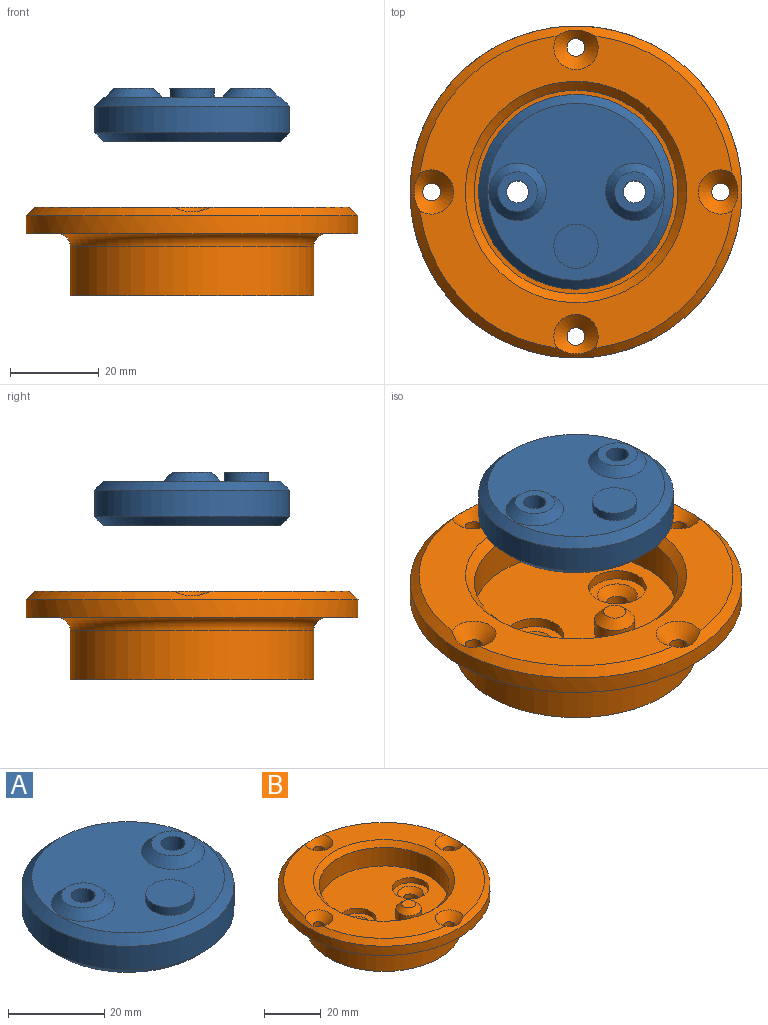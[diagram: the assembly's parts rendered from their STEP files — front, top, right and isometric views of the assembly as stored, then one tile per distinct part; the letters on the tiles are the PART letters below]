
ASSEMBLY  parts=2 mates=1
PART A: 22 faces, bbox 44x44x12 mm
  f0: cylinder r=5mm len=10mm, axis (0,0,-1), area 141.4mm2, adj f14,f15
  f1: cylinder r=6.5mm len=13mm, axis (0,0,-1), area 112.3mm2, adj f5,f11
  f2: cylinder r=6.5mm len=13mm, axis (0,0,-1), area 112.3mm2, adj f5,f8
  f3: cylinder r=22mm len=44mm, axis (0,0,-1), area 829.4mm2, adj f18,f19
  f4: plane 40x40mm, normal (0,0,1), area 912.6mm2, adj f13,f19,f20,f21
  f5: plane 40x40mm, normal (0,0,-1), area 837.2mm2, adj f1,f2,f15,f18
  f6: cylinder r=2.5mm len=7.25mm, axis (0,0,-1), area 113.9mm2, adj f7,f17
  f7: plane 9x9mm, normal (0,0,1), area 44mm2, adj f6,f20
  f8: plane 13x13mm, normal (0,0,-1), area 69.1mm2, adj f2,f17
  f9: cylinder r=2.5mm len=7.25mm, axis (0,0,-1), area 113.9mm2, adj f10,f16
  f10: plane 9x9mm, normal (0,0,1), area 44mm2, adj f9,f21
  f11: plane 13x13mm, normal (0,0,-1), area 69.1mm2, adj f1,f16
  f12: plane 10x10mm, normal (0,0,1), area 78.5mm2, adj f13
  f13: cylinder r=5mm len=10mm, axis (0,0,-1), area 62.8mm2, adj f4,f12
  f14: plane 10x10mm, normal (0,0,-1), area 78.5mm2, adj f0
  f15: cone r=7mm half-angle=45deg, axis (0,0,-1), area 106.6mm2, adj f0,f5
  f16: cone r=4.5mm half-angle=45deg, axis (0,0,-1), area 62.2mm2, adj f9,f11
  f17: cone r=4.5mm half-angle=45deg, axis (0,0,-1), area 62.2mm2, adj f6,f8
  f18: cone r=22mm half-angle=45deg, axis (0,0,1), area 373.2mm2, adj f3,f5
  f19: cone r=20mm half-angle=45deg, axis (0,0,-1), area 373.2mm2, adj f3,f4
  f20: cone r=4.5mm half-angle=45deg, axis (0,0,-1), area 97.7mm2, adj f4,f7
  f21: cone r=4.5mm half-angle=45deg, axis (0,0,-1), area 97.7mm2, adj f4,f10
PART B: 29 faces, bbox 75.3x75.3x20 mm
  f0: cylinder r=27.5mm len=55mm, axis (0,0,-1), area 1900.7mm2, adj f3,f28
  f1: cylinder r=23mm len=46mm, axis (0,0,-1), area 1156.1mm2, adj f6,f22
  f2: plane 70.48x70.48mm, normal (0,0,1), area 1733.9mm2, adj f21,f22,f24,f25,f26,f27
  f3: plane 55x55mm, normal (0,0,-1), area 2336.6mm2, adj f0,f7,f9
  f4: cylinder r=6.5mm len=13mm, axis (0,0,-1), area 91.9mm2, adj f6,f8
  f5: cylinder r=6.5mm len=13mm, axis (0,0,-1), area 91.9mm2, adj f6,f10
  f6: plane 46x46mm, normal (0,0,1), area 1332.8mm2, adj f1,f4,f5,f18
  f7: cylinder r=2.5mm len=5.75mm, axis (0,0,-1), area 90.3mm2, adj f3,f20
  f8: plane 13x13mm, normal (0,0,1), area 69.1mm2, adj f4,f20
  f9: cylinder r=2.5mm len=5.75mm, axis (0,0,-1), area 90.3mm2, adj f3,f19
  f10: plane 13x13mm, normal (0,0,1), area 69.1mm2, adj f5,f19
  f11: cylinder r=2mm len=4mm, axis (0,0,-1), area 37.7mm2, adj f16,f26
  f12: cylinder r=2mm len=4mm, axis (0,0,-1), area 37.7mm2, adj f16,f27
  f13: cylinder r=2mm len=4mm, axis (0,0,-1), area 37.7mm2, adj f16,f24
  f14: cylinder r=2mm len=4mm, axis (0,0,-1), area 37.7mm2, adj f16,f25
  f15: cylinder r=37.5mm len=75mm, axis (0,0,-1), area 942.5mm2, adj f16,f21
  f16: plane 75x75mm, normal (0,0,-1), area 1445.1mm2, adj f11,f12,f13,f14,f15,f28
  f17: plane 5x5mm, normal (0,0,1), area 19.6mm2, adj f23
  f18: cylinder r=4.5mm len=9mm, axis (0,0,-1), area 113.1mm2, adj f6,f23
  f19: cone r=2.5mm half-angle=45deg, axis (0,0,1), area 62.2mm2, adj f9,f10
  f20: cone r=2.5mm half-angle=45deg, axis (0,0,1), area 62.2mm2, adj f7,f8
  f21: cone r=35.5mm half-angle=45deg, axis (0,0,-1), area 613.7mm2, adj f2,f15,f24,f25,f26,f27
  f22: cone r=23mm half-angle=45deg, axis (0,0,1), area 426.5mm2, adj f1,f2
  f23: cone r=2.5mm half-angle=45deg, axis (0,0,-1), area 62.2mm2, adj f17,f18
  f24: cone r=2mm half-angle=45deg, axis (0,0,1), area 83.5mm2, adj f2,f13,f21
  f25: cone r=2mm half-angle=45deg, axis (0,0,1), area 83.5mm2, adj f2,f14,f21
  f26: cone r=2mm half-angle=45deg, axis (0,0,1), area 83.5mm2, adj f2,f11,f21
  f27: cone r=2mm half-angle=45deg, axis (0,0,1), area 83.5mm2, adj f2,f12,f21
  f28: torus R=30.5mm, axis (0,0,1), area 846.5mm2, adj f0,f16
PLACE A t=(-27.14,7.22,31.06)mm
PLACE B t=(-27.14,8.17,-3.72)mm
MATE slider A.f0 <-> B.f18  axis (0,0,-1) through (-27.14,-4.12,37.56)mm
